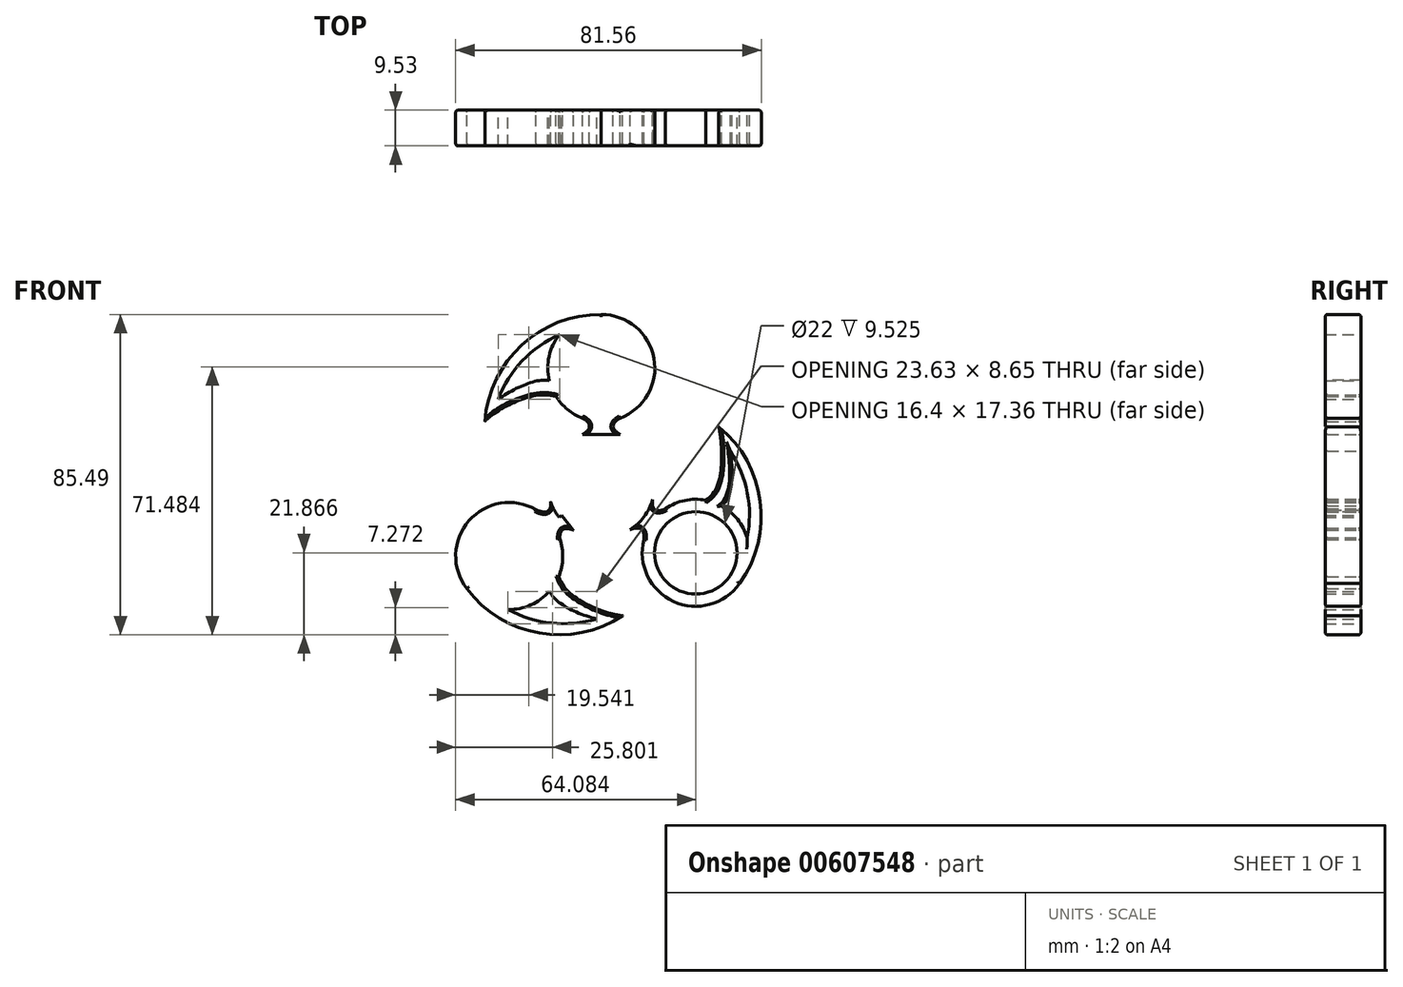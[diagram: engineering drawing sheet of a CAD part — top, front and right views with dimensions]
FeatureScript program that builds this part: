
annotation { "Feature Type Name" : "Feature", "Feature Type Description" : "" }
export const myFeature = defineFeature(function(context is Context, id is Id, definition is map)
    precondition{}
    {
        {
            var Q0;
            Q0=qCreatedBy(makeId("Front.planeOp"),FACE);
            var sketch = newSketch(context, id + "F0", { "sketchPlane" : qUnion([Q0])});
            skCircle(sketch, "E0", {"center": v(0, 0) * mm, "radius": 14.29 * mm});
            skLineSegment(sketch, "E1", {"start": v(0, 0) * mm, "end": v(0, 14.29) * mm});
            skLineSegment(sketch, "E2", {"start": v(0, 0) * mm, "end": v(-11.3, -8.76) * mm});
            skLineSegment(sketch, "E3", {"start": v(0, 0) * mm, "end": v(11.43, -8.57) * mm});
            skCircle(sketch, "E4", {"center": v(0, 31.12) * mm, "radius": 14.29 * mm});
            skLineSegment(sketch, "E5", {"start": v(0, 14.29) * mm, "end": v(0, 16.83) * mm});
            skArc(sketch, "E6", {"start": v(0, 45.4) * mm, "mid": v(-21.2, 37.27) * mm, "end": v(-31.1, 16.83) * mm});
            skFitSpline(sketch, "E7", {"points": [v(-31.1, 16.83) * mm, v(-17.35, 23.79) * mm, v(0, 16.83) * mm], "startDerivative": vector(18.3, 19.68) * mm, "endDerivative": vector(52.34, -33.11) * mm});
            skLineSegment(sketch, "E8", {"start": v(0, 15.56) * mm, "end": v(-3.18, 15.56) * mm});
            skPoint(sketch, "E8.endSnap0", {"position": v(0, 15.56) * mm});
            skLineSegment(sketch, "E9", {"start": v(0, 15.56) * mm, "end": v(3.18, 15.56) * mm});
            skLineSegment(sketch, "E10", {"start": v(0, 17.74) * mm, "end": v(5.03, 17.74) * mm});
            skLineSegment(sketch, "E11", {"start": v(0, 17.74) * mm, "end": v(-5.03, 17.74) * mm});
            skLineSegment(sketch, "E12", {"start": v(0, 14.29) * mm, "end": v(0, 13.37) * mm});
            skLineSegment(sketch, "E13", {"start": v(0, 13.37) * mm, "end": v(-5.03, 13.37) * mm});
            skLineSegment(sketch, "E14", {"start": v(0, 13.37) * mm, "end": v(5.03, 13.37) * mm});
            skFitSpline(sketch, "E15", {"points": [v(-5.03, 17.74) * mm, v(-3.18, 15.56) * mm, v(-5.03, 13.37) * mm], "startDerivative": vector(7.47, -4.37) * mm, "endDerivative": vector(-7.47, -4.37) * mm});
            skFitSpline(sketch, "E16", {"points": [v(5.03, 13.37) * mm, v(3.18, 15.56) * mm, v(5.03, 17.74) * mm], "startDerivative": vector(-7.47, 4.37) * mm, "endDerivative": vector(7.47, 4.37) * mm});
            skArc(sketch, "E17", {"start": v(4.36, 42.56) * mm, "mid": v(-16.61, 36.94) * mm, "end": v(-28.69, 18.9) * mm});
            skFitSpline(sketch, "E18", {"points": [v(-30.7, 19.98) * mm, v(-16.8, 27.72) * mm, v(0.44, 19.97) * mm], "startDerivative": vector(18.3, 19.68) * mm, "endDerivative": vector(52.34, -33.11) * mm});
            skLineSegment(sketch, "E19", {"start": v(-3.18, 15.56) * mm, "end": v(0, 14.29) * mm});
            skLineSegment(sketch, "E20", {"start": v(0, 14.29) * mm, "end": v(3.18, 15.56) * mm});
            skCircle(sketch, "E21", {"center": v(25.21, -18.22) * mm, "radius": 14.29 * mm});
            skLineSegment(sketch, "E22", {"start": v(11.43, -8.57) * mm, "end": v(13.51, -10.03) * mm});
            skArc(sketch, "E23", {"start": v(36.92, -26.42) * mm, "mid": v(42.42, -4.39) * mm, "end": v(31.34, 15.44) * mm});
            skFitSpline(sketch, "E24", {"points": [v(31.34, 15.44) * mm, v(30.71, -0.93) * mm, v(13.51, -10.03) * mm], "startDerivative": vector(5.62, -26.28) * mm, "endDerivative": vector(-57.15, -23.88) * mm});
            skLineSegment(sketch, "E25", {"start": v(12.47, -9.3) * mm, "end": v(14.3, -6.7) * mm});
            skPoint(sketch, "E25.endSnap0", {"position": v(12.47, -9.3) * mm});
            skLineSegment(sketch, "E26", {"start": v(12.47, -9.3) * mm, "end": v(10.65, -11.9) * mm});
            skLineSegment(sketch, "E27", {"start": v(14.26, -10.55) * mm, "end": v(11.38, -14.67) * mm});
            skLineSegment(sketch, "E28", {"start": v(14.26, -10.55) * mm, "end": v(17.14, -6.43) * mm});
            skArc(sketch, "E29", {"start": v(32.04, -28.23) * mm, "mid": v(39.54, -7.93) * mm, "end": v(31.84, 12.3) * mm});
            skFitSpline(sketch, "E30", {"points": [v(33.7, 13.3) * mm, v(33.83, -3.4) * mm, v(15.84, -12.2) * mm], "startDerivative": vector(5.62, -26.28) * mm, "endDerivative": vector(-57.15, -23.88) * mm});
            skLineSegment(sketch, "E31", {"start": v(14.3, -6.7) * mm, "end": v(11.8, -8.05) * mm});
            skLineSegment(sketch, "E32", {"start": v(11.43, -8.57) * mm, "end": v(10.65, -11.9) * mm});
            skLineSegment(sketch, "E33.0", {"start": v(14.3, -6.7) * mm, "end": v(12.47, -9.3) * mm, "construction": true});
            skCircle(sketch, "E34", {"center": v(-24.58, -19.07) * mm, "radius": 14.29 * mm});
            skLineSegment(sketch, "E35", {"start": v(-11.3, -8.76) * mm, "end": v(-13.26, -10.36) * mm});
            skArc(sketch, "E36", {"start": v(-35.91, -27.78) * mm, "mid": v(-16.54, -39.63) * mm, "end": v(5.7, -35.02) * mm});
            skFitSpline(sketch, "E37", {"points": [v(5.7, -35.02) * mm, v(-8.63, -28.76) * mm, v(-13.26, -10.36) * mm], "startDerivative": vector(-26.76, 2.52) * mm, "endDerivative": vector(-5.64, 61.68) * mm});
            skLineSegment(sketch, "E38", {"start": v(-12.27, -9.56) * mm, "end": v(-10.26, -12.02) * mm});
            skPoint(sketch, "E38.endSnap0", {"position": v(-12.27, -9.56) * mm});
            skLineSegment(sketch, "E39", {"start": v(-12.27, -9.56) * mm, "end": v(-14.28, -7.1) * mm});
            skLineSegment(sketch, "E40", {"start": v(-13.97, -10.94) * mm, "end": v(-17.43, -6.7) * mm});
            skLineSegment(sketch, "E41", {"start": v(-13.97, -10.94) * mm, "end": v(-11.04, -14.51) * mm});
            skArc(sketch, "E42", {"start": v(-36.27, -22.58) * mm, "mid": v(-19.07, -35.8) * mm, "end": v(2.57, -34.43) * mm});
            skFitSpline(sketch, "E43", {"points": [v(2.95, -36.62) * mm, v(-12.05, -30.77) * mm, v(-16.16, -11.65) * mm], "startDerivative": vector(-26.76, 2.52) * mm, "endDerivative": vector(-5.64, 61.68) * mm});
            skLineSegment(sketch, "E44", {"start": v(-10.26, -12.02) * mm, "end": v(-10.8, -9.23) * mm});
            skLineSegment(sketch, "E45", {"start": v(-11.3, -8.76) * mm, "end": v(-14.28, -7.1) * mm});
            skLineSegment(sketch, "E46.0", {"start": v(-10.26, -12.02) * mm, "end": v(-12.27, -9.56) * mm, "construction": true});
            skLineSegment(sketch, "E47", {"start": v(-11.3, -8.76) * mm, "end": v(-10.57, -8.2) * mm});
            skLineSegment(sketch, "E48", {"start": v(11.43, -8.57) * mm, "end": v(10.7, -8.02) * mm});
            skLineSegment(sketch, "E49", {"start": v(10.7, -8.02) * mm, "end": v(13.72, -4) * mm});
            skLineSegment(sketch, "E50", {"start": v(10.7, -8.02) * mm, "end": v(7.68, -12.05) * mm});
            skLineSegment(sketch, "E51", {"start": v(-10.57, -8.2) * mm, "end": v(-13.54, -4.56) * mm});
            skLineSegment(sketch, "E52", {"start": v(-10.57, -8.2) * mm, "end": v(-7.49, -12.17) * mm});
            skFitSpline(sketch, "E53", {"points": [v(-13.54, -4.56) * mm, v(-14.28, -7.1) * mm, v(-17.43, -6.7) * mm], "startDerivative": vector(0.73, -8.28) * mm, "endDerivative": vector(-8.38, 3.81) * mm});
            skFitSpline(sketch, "E54", {"points": [v(-11.04, -14.51) * mm, v(-10.26, -12.02) * mm, v(-7.49, -12.17) * mm], "startDerivative": vector(-0.57, 7.9) * mm, "endDerivative": vector(7.64, -3.14) * mm});
            skFitSpline(sketch, "E55", {"points": [v(7.68, -12.05) * mm, v(10.65, -11.9) * mm, v(11.38, -14.67) * mm], "startDerivative": vector(8.1, 3.32) * mm, "endDerivative": vector(-0.74, -8.6) * mm});
            skFitSpline(sketch, "E56", {"points": [v(13.72, -4) * mm, v(14.3, -6.7) * mm, v(17.14, -6.43) * mm], "startDerivative": vector(-1.06, -8.48) * mm, "endDerivative": vector(7.9, 3.59) * mm});
            skSolve(sketch);
        }
        {
            var Q0;
            {var subQ0=sQuery(id+"F0.wireOp",EDGE,"E6");var subQ1=sQuery(id+"F0.wireOp",EDGE,"E4");var subQ2=makeQuery(id+"F0.imprint","INTERSECT",VERTEX,{"derivedFrom":[subQ1,subQ0]});Q0=makeQuery(id+"F0.imprint","IMPRINT",FACE,{"disambiguationData":[TD([[makeQuery(id+"F0.imprint","IMPRINT",EDGE,{"disambiguationData":[TD([[subQ2,-1.0]])],"derivedFrom":subQ1}),-1.0]])]});}
            var Q1;
            {var subQ0=sQuery(id+"F0.wireOp",EDGE,"E18");var subQ1=sQuery(id+"F0.wireOp",EDGE,"E4");var subQ2=makeQuery(id+"F0.imprint","INTERSECT",VERTEX,{"derivedFrom":[subQ1,subQ0]});Q1=makeQuery(id+"F0.imprint","IMPRINT",FACE,{"disambiguationData":[TD([[makeQuery(id+"F0.imprint","IMPRINT",EDGE,{"disambiguationData":[TD([[subQ2,-1.0]])],"derivedFrom":subQ1}),-1.0]])]});}
            var Q2;
            {var subQ0=sQuery(id+"F0.wireOp",EDGE,"E7");var subQ1=sQuery(id+"F0.wireOp",EDGE,"E6");var subQ2=makeQuery(id+"F0.imprint","INTERSECT",VERTEX,{"derivedFrom":[subQ1,subQ0]});Q2=makeQuery(id+"F0.imprint","IMPRINT",FACE,{"disambiguationData":[TD([[makeQuery(id+"F0.imprint","IMPRINT",EDGE,{"disambiguationData":[TD([[subQ2,1.0]])],"derivedFrom":subQ1}),1.0]])]});}
            var Q3;
            {var subQ7=sQuery(id+"F0.wireOp",EDGE,"E10");Q3=makeQuery(id+"F0.imprint","IMPRINT",FACE,{"disambiguationData":[TD([[makeQuery(id+"F0.imprint","IMPRINT",EDGE,{"derivedFrom":subQ7}),1.0]])]});}
            var Q4;
            Q4=makeQuery(id+"F0.imprint","IMPRINT",FACE,{"disambiguationData":[TD([[makeQuery(id+"F0.imprint","IMPRINT",EDGE,{"derivedFrom":sQuery(id+"F0.wireOp",EDGE,"E1")}),1.0]])]});
            var Q5;
            Q5=makeQuery(id+"F0.imprint","IMPRINT",FACE,{"disambiguationData":[TD([[makeQuery(id+"F0.imprint","IMPRINT",EDGE,{"derivedFrom":sQuery(id+"F0.wireOp",EDGE,"E2")}),1.0]])]});
            var Q6;
            Q6=makeQuery(id+"F0.imprint","IMPRINT",FACE,{"disambiguationData":[TD([[makeQuery(id+"F0.imprint","IMPRINT",EDGE,{"derivedFrom":sQuery(id+"F0.wireOp",EDGE,"E1")}),-1.0]])]});
            var Q7;
            {var subQ7=sQuery(id+"F0.wireOp",EDGE,"E40");Q7=makeQuery(id+"F0.imprint","IMPRINT",FACE,{"disambiguationData":[TD([[makeQuery(id+"F0.imprint","IMPRINT",EDGE,{"derivedFrom":subQ7}),1.0]])]});}
            var Q8;
            {var subQ0=sQuery(id+"F0.wireOp",EDGE,"E36");var subQ1=sQuery(id+"F0.wireOp",EDGE,"E34");var subQ2=makeQuery(id+"F0.imprint","INTERSECT",VERTEX,{"derivedFrom":[subQ1,subQ0]});Q8=makeQuery(id+"F0.imprint","IMPRINT",FACE,{"disambiguationData":[TD([[makeQuery(id+"F0.imprint","IMPRINT",EDGE,{"disambiguationData":[TD([[subQ2,-1.0]])],"derivedFrom":subQ1}),-1.0]])]});}
            var Q9;
            {var subQ0=sQuery(id+"F0.wireOp",EDGE,"E43");var subQ1=sQuery(id+"F0.wireOp",EDGE,"E34");var subQ2=makeQuery(id+"F0.imprint","INTERSECT",VERTEX,{"derivedFrom":[subQ1,subQ0]});Q9=makeQuery(id+"F0.imprint","IMPRINT",FACE,{"disambiguationData":[TD([[makeQuery(id+"F0.imprint","IMPRINT",EDGE,{"disambiguationData":[TD([[subQ2,-1.0]])],"derivedFrom":subQ1}),-1.0]])]});}
            var Q10;
            {var subQ0=sQuery(id+"F0.wireOp",EDGE,"E37");var subQ1=sQuery(id+"F0.wireOp",EDGE,"E36");var subQ2=makeQuery(id+"F0.imprint","INTERSECT",VERTEX,{"derivedFrom":[subQ1,subQ0]});Q10=makeQuery(id+"F0.imprint","IMPRINT",FACE,{"disambiguationData":[TD([[makeQuery(id+"F0.imprint","IMPRINT",EDGE,{"disambiguationData":[TD([[subQ2,1.0]])],"derivedFrom":subQ1}),1.0]])]});}
            var Q11;
            {var subQ1=sQuery(id+"F0.wireOp",EDGE,"E34");var subQ3=sQuery(id+"F0.wireOp",EDGE,"E37");var subQ4=makeQuery(id+"F0.imprint","INTERSECT",VERTEX,{"derivedFrom":[subQ1,subQ3]});Q11=makeQuery(id+"F0.imprint","IMPRINT",FACE,{"disambiguationData":[TD([[makeQuery(id+"F0.imprint","IMPRINT",EDGE,{"disambiguationData":[TD([[subQ4,-1.0]])],"derivedFrom":subQ3}),-1.0]])]});}
            var Q12;
            {var subQ5=sQuery(id+"F0.wireOp",EDGE,"E27");Q12=makeQuery(id+"F0.imprint","IMPRINT",FACE,{"disambiguationData":[TD([[makeQuery(id+"F0.imprint","IMPRINT",EDGE,{"derivedFrom":subQ5}),1.0]])]});}
            var Q13;
            {var subQ0=sQuery(id+"F0.wireOp",EDGE,"E23");var subQ1=sQuery(id+"F0.wireOp",EDGE,"E21");var subQ2=makeQuery(id+"F0.imprint","INTERSECT",VERTEX,{"derivedFrom":[subQ1,subQ0]});Q13=makeQuery(id+"F0.imprint","IMPRINT",FACE,{"disambiguationData":[TD([[makeQuery(id+"F0.imprint","IMPRINT",EDGE,{"disambiguationData":[TD([[subQ2,-1.0]])],"derivedFrom":subQ1}),-1.0]])]});}
            var Q14;
            {var subQ0=sQuery(id+"F0.wireOp",EDGE,"E30");var subQ1=sQuery(id+"F0.wireOp",EDGE,"E21");var subQ2=makeQuery(id+"F0.imprint","INTERSECT",VERTEX,{"derivedFrom":[subQ1,subQ0]});Q14=makeQuery(id+"F0.imprint","IMPRINT",FACE,{"disambiguationData":[TD([[makeQuery(id+"F0.imprint","IMPRINT",EDGE,{"disambiguationData":[TD([[subQ2,-1.0]])],"derivedFrom":subQ1}),-1.0]])]});}
            var Q15;
            {var subQ0=sQuery(id+"F0.wireOp",EDGE,"E24");var subQ1=sQuery(id+"F0.wireOp",EDGE,"E23");var subQ2=makeQuery(id+"F0.imprint","INTERSECT",VERTEX,{"derivedFrom":[subQ1,subQ0]});Q15=makeQuery(id+"F0.imprint","IMPRINT",FACE,{"disambiguationData":[TD([[makeQuery(id+"F0.imprint","IMPRINT",EDGE,{"disambiguationData":[TD([[subQ2,1.0]])],"derivedFrom":subQ1}),1.0]])]});}
            var Q16;
            {var subQ0=sQuery(id+"F0.wireOp",EDGE,"E28");var subQ1=sQuery(id+"F0.wireOp",EDGE,"E21");var subQ2=makeQuery(id+"F0.imprint","INTERSECT",VERTEX,{"derivedFrom":[subQ1,subQ0]});Q16=makeQuery(id+"F0.imprint","IMPRINT",FACE,{"disambiguationData":[TD([[makeQuery(id+"F0.imprint","IMPRINT",EDGE,{"disambiguationData":[TD([[subQ2,1.0]])],"derivedFrom":subQ1}),1.0]])]});}
            var Q17;
            {var subQ3=sQuery(id+"F0.wireOp",EDGE,"E40");Q17=makeQuery(id+"F0.imprint","IMPRINT",FACE,{"disambiguationData":[TD([[makeQuery(id+"F0.imprint","IMPRINT",EDGE,{"derivedFrom":subQ3}),-1.0]])]});}
            var Q18;
            {var subQ0=sQuery(id+"F0.wireOp",EDGE,"E37");var subQ3=sQuery(id+"F0.wireOp",EDGE,"E41");var subQ5=makeQuery(id+"F0.imprint","INTERSECT",VERTEX,{"derivedFrom":[subQ0,subQ3]});Q18=makeQuery(id+"F0.imprint","IMPRINT",FACE,{"disambiguationData":[TD([[makeQuery(id+"F0.imprint","IMPRINT",EDGE,{"disambiguationData":[TD([[subQ5,-1.0]])],"derivedFrom":subQ0}),-1.0]])]});}
            var Q19;
            {var subQ0=sQuery(id+"F0.wireOp",EDGE,"E47");Q19=makeQuery(id+"F0.imprint","IMPRINT",FACE,{"disambiguationData":[TD([[makeQuery(id+"F0.imprint","IMPRINT",EDGE,{"derivedFrom":subQ0}),-1.0]])]});}
            var Q20;
            {var subQ0=sQuery(id+"F0.wireOp",EDGE,"E47");Q20=makeQuery(id+"F0.imprint","IMPRINT",FACE,{"disambiguationData":[TD([[makeQuery(id+"F0.imprint","IMPRINT",EDGE,{"derivedFrom":subQ0}),1.0]])]});}
            var Q21;
            {var subQ0=sQuery(id+"F0.wireOp",EDGE,"E45");Q21=makeQuery(id+"F0.imprint","IMPRINT",FACE,{"disambiguationData":[TD([[makeQuery(id+"F0.imprint","IMPRINT",EDGE,{"derivedFrom":subQ0}),-1.0]])]});}
            var Q22;
            {var subQ1=sQuery(id+"F0.wireOp",EDGE,"E0");var subQ3=sQuery(id+"F0.wireOp",EDGE,"E44");var subQ4=makeQuery(id+"F0.imprint","INTERSECT",VERTEX,{"derivedFrom":[subQ1,subQ3]});Q22=makeQuery(id+"F0.imprint","IMPRINT",FACE,{"disambiguationData":[TD([[makeQuery(id+"F0.imprint","IMPRINT",EDGE,{"disambiguationData":[TD([[subQ4,-1.0]])],"derivedFrom":subQ1}),-1.0]])]});}
            var Q23;
            {var subQ5=sQuery(id+"F0.wireOp",EDGE,"E38");Q23=makeQuery(id+"F0.imprint","IMPRINT",FACE,{"disambiguationData":[TD([[makeQuery(id+"F0.imprint","IMPRINT",EDGE,{"derivedFrom":subQ5}),-1.0]])]});}
            var Q24;
            {var subQ5=sQuery(id+"F0.wireOp",EDGE,"E39");Q24=makeQuery(id+"F0.imprint","IMPRINT",FACE,{"disambiguationData":[TD([[makeQuery(id+"F0.imprint","IMPRINT",EDGE,{"derivedFrom":subQ5}),1.0]])]});}
            var Q25;
            {var subQ2=sQuery(id+"F0.wireOp",EDGE,"E39");Q25=makeQuery(id+"F0.imprint","IMPRINT",FACE,{"disambiguationData":[TD([[makeQuery(id+"F0.imprint","IMPRINT",EDGE,{"derivedFrom":subQ2}),-1.0]])]});}
            var Q26;
            {var subQ5=sQuery(id+"F0.wireOp",EDGE,"E38");Q26=makeQuery(id+"F0.imprint","IMPRINT",FACE,{"disambiguationData":[TD([[makeQuery(id+"F0.imprint","IMPRINT",EDGE,{"derivedFrom":subQ5}),1.0]])]});}
            var Q27;
            {var subQ3=sQuery(id+"F0.wireOp",EDGE,"E27");Q27=makeQuery(id+"F0.imprint","IMPRINT",FACE,{"disambiguationData":[TD([[makeQuery(id+"F0.imprint","IMPRINT",EDGE,{"derivedFrom":subQ3}),-1.0]])]});}
            var Q28;
            {var subQ0=sQuery(id+"F0.wireOp",EDGE,"E24");var subQ3=sQuery(id+"F0.wireOp",EDGE,"E28");var subQ5=makeQuery(id+"F0.imprint","INTERSECT",VERTEX,{"derivedFrom":[subQ0,subQ3]});Q28=makeQuery(id+"F0.imprint","IMPRINT",FACE,{"disambiguationData":[TD([[makeQuery(id+"F0.imprint","IMPRINT",EDGE,{"disambiguationData":[TD([[subQ5,-1.0]])],"derivedFrom":subQ0}),-1.0]])]});}
            var Q29;
            {var subQ5=sQuery(id+"F0.wireOp",EDGE,"E25");Q29=makeQuery(id+"F0.imprint","IMPRINT",FACE,{"disambiguationData":[TD([[makeQuery(id+"F0.imprint","IMPRINT",EDGE,{"derivedFrom":subQ5}),-1.0]])]});}
            var Q30;
            {var subQ2=sQuery(id+"F0.wireOp",EDGE,"E25");Q30=makeQuery(id+"F0.imprint","IMPRINT",FACE,{"disambiguationData":[TD([[makeQuery(id+"F0.imprint","IMPRINT",EDGE,{"derivedFrom":subQ2}),1.0]])]});}
            var Q31;
            {var subQ0=sQuery(id+"F0.wireOp",EDGE,"E31");Q31=makeQuery(id+"F0.imprint","IMPRINT",FACE,{"disambiguationData":[TD([[makeQuery(id+"F0.imprint","IMPRINT",EDGE,{"derivedFrom":subQ0}),-1.0]])]});}
            var Q32;
            {var subQ0=sQuery(id+"F0.wireOp",EDGE,"E48");Q32=makeQuery(id+"F0.imprint","IMPRINT",FACE,{"disambiguationData":[TD([[makeQuery(id+"F0.imprint","IMPRINT",EDGE,{"derivedFrom":subQ0}),-1.0]])]});}
            var Q33;
            {var subQ0=sQuery(id+"F0.wireOp",EDGE,"E48");Q33=makeQuery(id+"F0.imprint","IMPRINT",FACE,{"disambiguationData":[TD([[makeQuery(id+"F0.imprint","IMPRINT",EDGE,{"derivedFrom":subQ0}),1.0]])]});}
            var Q34;
            {var subQ0=sQuery(id+"F0.wireOp",EDGE,"E32");Q34=makeQuery(id+"F0.imprint","IMPRINT",FACE,{"disambiguationData":[TD([[makeQuery(id+"F0.imprint","IMPRINT",EDGE,{"derivedFrom":subQ0}),-1.0]])]});}
            var Q35;
            {var subQ2=sQuery(id+"F0.wireOp",EDGE,"E26");Q35=makeQuery(id+"F0.imprint","IMPRINT",FACE,{"disambiguationData":[TD([[makeQuery(id+"F0.imprint","IMPRINT",EDGE,{"derivedFrom":subQ2}),-1.0]])]});}
            var Q36;
            {var subQ5=sQuery(id+"F0.wireOp",EDGE,"E26");Q36=makeQuery(id+"F0.imprint","IMPRINT",FACE,{"disambiguationData":[TD([[makeQuery(id+"F0.imprint","IMPRINT",EDGE,{"derivedFrom":subQ5}),1.0]])]});}
            var Q37;
            {var subQ1=sQuery(id+"F0.wireOp",EDGE,"E4");var subQ3=sQuery(id+"F0.wireOp",EDGE,"E7");var subQ4=makeQuery(id+"F0.imprint","INTERSECT",VERTEX,{"derivedFrom":[subQ1,subQ3]});Q37=makeQuery(id+"F0.imprint","IMPRINT",FACE,{"disambiguationData":[TD([[makeQuery(id+"F0.imprint","IMPRINT",EDGE,{"disambiguationData":[TD([[subQ4,-1.0]])],"derivedFrom":subQ3}),-1.0]])]});}
            var Q38;
            {var subQ0=sQuery(id+"F0.wireOp",EDGE,"E7");var subQ3=sQuery(id+"F0.wireOp",EDGE,"E11");var subQ5=makeQuery(id+"F0.imprint","INTERSECT",VERTEX,{"derivedFrom":[subQ0,subQ3]});Q38=makeQuery(id+"F0.imprint","IMPRINT",FACE,{"disambiguationData":[TD([[makeQuery(id+"F0.imprint","IMPRINT",EDGE,{"disambiguationData":[TD([[subQ5,-1.0]])],"derivedFrom":subQ0}),-1.0]])]});}
            var Q39;
            {var subQ5=sQuery(id+"F0.wireOp",EDGE,"E8");Q39=makeQuery(id+"F0.imprint","IMPRINT",FACE,{"disambiguationData":[TD([[makeQuery(id+"F0.imprint","IMPRINT",EDGE,{"derivedFrom":subQ5}),-1.0]])]});}
            var Q40;
            {var subQ0=sQuery(id+"F0.wireOp",EDGE,"E20");Q40=makeQuery(id+"F0.imprint","IMPRINT",FACE,{"disambiguationData":[TD([[makeQuery(id+"F0.imprint","IMPRINT",EDGE,{"derivedFrom":subQ0}),-1.0]])]});}
            var Q41;
            {var subQ0=sQuery(id+"F0.wireOp",EDGE,"E12");Q41=makeQuery(id+"F0.imprint","IMPRINT",FACE,{"disambiguationData":[TD([[makeQuery(id+"F0.imprint","IMPRINT",EDGE,{"derivedFrom":subQ0}),1.0]])]});}
            var Q42;
            {var subQ0=sQuery(id+"F0.wireOp",EDGE,"E12");Q42=makeQuery(id+"F0.imprint","IMPRINT",FACE,{"disambiguationData":[TD([[makeQuery(id+"F0.imprint","IMPRINT",EDGE,{"derivedFrom":subQ0}),-1.0]])]});}
            var Q43;
            {var subQ0=sQuery(id+"F0.wireOp",EDGE,"E19");Q43=makeQuery(id+"F0.imprint","IMPRINT",FACE,{"disambiguationData":[TD([[makeQuery(id+"F0.imprint","IMPRINT",EDGE,{"derivedFrom":subQ0}),-1.0]])]});}
            var Q44;
            {var subQ2=sQuery(id+"F0.wireOp",EDGE,"E8");Q44=makeQuery(id+"F0.imprint","IMPRINT",FACE,{"disambiguationData":[TD([[makeQuery(id+"F0.imprint","IMPRINT",EDGE,{"derivedFrom":subQ2}),1.0]])]});}
            var Q45;
            {var subQ2=sQuery(id+"F0.wireOp",EDGE,"E9");Q45=makeQuery(id+"F0.imprint","IMPRINT",FACE,{"disambiguationData":[TD([[makeQuery(id+"F0.imprint","IMPRINT",EDGE,{"derivedFrom":subQ2}),-1.0]])]});}
            var Q46;
            {var subQ5=sQuery(id+"F0.wireOp",EDGE,"E9");Q46=makeQuery(id+"F0.imprint","IMPRINT",FACE,{"disambiguationData":[TD([[makeQuery(id+"F0.imprint","IMPRINT",EDGE,{"derivedFrom":subQ5}),1.0]])]});}
            var Q47;
            {var subQ3=sQuery(id+"F0.wireOp",EDGE,"E10");Q47=makeQuery(id+"F0.imprint","IMPRINT",FACE,{"disambiguationData":[TD([[makeQuery(id+"F0.imprint","IMPRINT",EDGE,{"derivedFrom":subQ3}),-1.0]])]});}
            extrude(context, id + "F1", {"entities" : qUnion([Q0, Q1, Q2, Q3, Q4, Q5, Q6, Q7, Q8, Q9, Q10, Q11, Q12, Q13, Q14, Q15, Q16, Q17, Q18, Q19, Q20, Q21, Q22, Q23, Q24, Q25, Q26, Q27, Q28, Q29, Q30, Q31, Q32, Q33, Q34, Q35, Q36, Q37, Q38, Q39, Q40, Q41, Q42, Q43, Q44, Q45, Q46, Q47]), "depth" : 9.52 * mm});
        }
        {
            var Q0;
            {var subQ0=sQuery(id+"F0.wireOp",EDGE,"E4");Q0=makeQuery(id+"F1.opExtrude","CAP_EDGE",EDGE,{"disambiguationData":[OSD([subQ0]),TDD([makeQuery(id+"F0.imprint","IMPRINT",EDGE,{"disambiguationData":[TD([[makeQuery(id+"F0.imprint","INTERSECT",VERTEX,{"derivedFrom":[subQ0,sQuery(id+"F0.wireOp",EDGE,"E7")]}),-1.0]])],"derivedFrom":subQ0})])],"isStart":false});}
            var Q1;
            Q1=makeQuery(id+"F1.opExtrude","CAP_EDGE",EDGE,{"disambiguationData":[OSD([sQuery(id+"F0.wireOp",EDGE,"E15")])],"isStart":false});
            var Q2;
            {var subQ0=sQuery(id+"F0.wireOp",EDGE,"E0");Q2=makeQuery(id+"F1.opExtrude","CAP_EDGE",EDGE,{"disambiguationData":[OSD([subQ0]),TDD([makeQuery(id+"F0.imprint","IMPRINT",EDGE,{"disambiguationData":[TD([[makeQuery(id+"F0.imprint","INTERSECT",VERTEX,{"derivedFrom":[subQ0,sQuery(id+"F0.wireOp",EDGE,"E13"),sQuery(id+"F0.wireOp",EDGE,"E15")]}),-1.0]])],"derivedFrom":subQ0})])],"isStart":false});}
            var Q3;
            Q3=makeQuery(id+"F1.opExtrude","CAP_EDGE",EDGE,{"disambiguationData":[OSD([sQuery(id+"F0.wireOp",EDGE,"E53")])],"isStart":false});
            var Q4;
            {var subQ0=sQuery(id+"F0.wireOp",EDGE,"E34");Q4=makeQuery(id+"F1.opExtrude","CAP_EDGE",EDGE,{"disambiguationData":[OSD([subQ0]),TDD([makeQuery(id+"F0.imprint","IMPRINT",EDGE,{"disambiguationData":[TD([[makeQuery(id+"F0.imprint","INTERSECT",VERTEX,{"derivedFrom":[subQ0,sQuery(id+"F0.wireOp",EDGE,"E36")]}),1.0]])],"derivedFrom":subQ0})])],"isStart":false});}
            var Q5;
            Q5=makeQuery(id+"F1.opExtrude","CAP_EDGE",EDGE,{"disambiguationData":[OSD([sQuery(id+"F0.wireOp",EDGE,"E36")])],"isStart":false});
            var Q6;
            Q6=makeQuery(id+"F1.opExtrude","CAP_EDGE",EDGE,{"disambiguationData":[OSD([sQuery(id+"F0.wireOp",EDGE,"E37")])],"isStart":false});
            var Q7;
            Q7=makeQuery(id+"F1.opExtrude","CAP_FACE",FACE,{"disambiguationData":[OSD([sQuery(id+"F0.wireOp",EDGE,"E0"),sQuery(id+"F0.wireOp",EDGE,"E4"),sQuery(id+"F0.wireOp",EDGE,"E6"),sQuery(id+"F0.wireOp",EDGE,"E7"),sQuery(id+"F0.wireOp",EDGE,"E15"),sQuery(id+"F0.wireOp",EDGE,"E16"),sQuery(id+"F0.wireOp",EDGE,"E17"),sQuery(id+"F0.wireOp",EDGE,"E18"),sQuery(id+"F0.wireOp",EDGE,"E21"),sQuery(id+"F0.wireOp",EDGE,"E23"),sQuery(id+"F0.wireOp",EDGE,"E24"),sQuery(id+"F0.wireOp",EDGE,"E29"),sQuery(id+"F0.wireOp",EDGE,"E30"),sQuery(id+"F0.wireOp",EDGE,"E34"),sQuery(id+"F0.wireOp",EDGE,"E36"),sQuery(id+"F0.wireOp",EDGE,"E37"),sQuery(id+"F0.wireOp",EDGE,"E42"),sQuery(id+"F0.wireOp",EDGE,"E43"),sQuery(id+"F0.wireOp",EDGE,"E53"),sQuery(id+"F0.wireOp",EDGE,"E54"),sQuery(id+"F0.wireOp",EDGE,"E55"),sQuery(id+"F0.wireOp",EDGE,"E56")])],"isStart":false});
            var Q8;
            Q8=makeQuery(id+"F1.opExtrude","CAP_EDGE",EDGE,{"disambiguationData":[OSD([sQuery(id+"F0.wireOp",EDGE,"E7")])],"isStart":false});
            var Q9;
            Q9=makeQuery(id+"F1.opExtrude","CAP_EDGE",EDGE,{"disambiguationData":[OSD([sQuery(id+"F0.wireOp",EDGE,"E54")])],"isStart":false});
            var Q10;
            {var subQ0=sQuery(id+"F0.wireOp",EDGE,"E34");Q10=makeQuery(id+"F1.opExtrude","CAP_EDGE",EDGE,{"disambiguationData":[OSD([subQ0]),TDD([makeQuery(id+"F0.imprint","IMPRINT",EDGE,{"disambiguationData":[TD([[makeQuery(id+"F0.imprint","INTERSECT",VERTEX,{"derivedFrom":[subQ0,sQuery(id+"F0.wireOp",EDGE,"E37")]}),-1.0]])],"derivedFrom":subQ0})])],"isStart":false});}
            var Q11;
            {var subQ0=sQuery(id+"F0.wireOp",EDGE,"E0");Q11=makeQuery(id+"F1.opExtrude","CAP_EDGE",EDGE,{"disambiguationData":[OSD([subQ0]),TDD([makeQuery(id+"F0.imprint","IMPRINT",EDGE,{"disambiguationData":[TD([[makeQuery(id+"F0.imprint","INTERSECT",VERTEX,{"derivedFrom":[subQ0,sQuery(id+"F0.wireOp",EDGE,"E50"),sQuery(id+"F0.wireOp",EDGE,"E55")]}),1.0]])],"derivedFrom":subQ0})])],"isStart":false});}
            var Q12;
            Q12=makeQuery(id+"F1.opExtrude","CAP_EDGE",EDGE,{"disambiguationData":[OSD([sQuery(id+"F0.wireOp",EDGE,"E55")])],"isStart":false});
            var Q13;
            {var subQ0=sQuery(id+"F0.wireOp",EDGE,"E21");Q13=makeQuery(id+"F1.opExtrude","CAP_EDGE",EDGE,{"disambiguationData":[OSD([subQ0]),TDD([makeQuery(id+"F0.imprint","IMPRINT",EDGE,{"disambiguationData":[TD([[makeQuery(id+"F0.imprint","INTERSECT",VERTEX,{"derivedFrom":[subQ0,sQuery(id+"F0.wireOp",EDGE,"E23")]}),1.0]])],"derivedFrom":subQ0})])],"isStart":false});}
            var Q14;
            Q14=makeQuery(id+"F1.opExtrude","CAP_EDGE",EDGE,{"disambiguationData":[OSD([sQuery(id+"F0.wireOp",EDGE,"E23")])],"isStart":false});
            var Q15;
            Q15=makeQuery(id+"F1.opExtrude","CAP_EDGE",EDGE,{"disambiguationData":[OSD([sQuery(id+"F0.wireOp",EDGE,"E24")])],"isStart":false});
            var Q16;
            {var subQ0=sQuery(id+"F0.wireOp",EDGE,"E21");Q16=makeQuery(id+"F1.opExtrude","CAP_EDGE",EDGE,{"disambiguationData":[OSD([subQ0]),TDD([makeQuery(id+"F0.imprint","IMPRINT",EDGE,{"disambiguationData":[TD([[makeQuery(id+"F0.imprint","INTERSECT",VERTEX,{"derivedFrom":[subQ0,sQuery(id+"F0.wireOp",EDGE,"E24")]}),-1.0]])],"derivedFrom":subQ0})])],"isStart":false});}
            var Q17;
            Q17=makeQuery(id+"F1.opExtrude","CAP_EDGE",EDGE,{"disambiguationData":[OSD([sQuery(id+"F0.wireOp",EDGE,"E56")])],"isStart":false});
            var Q18;
            {var subQ0=sQuery(id+"F0.wireOp",EDGE,"E0");Q18=makeQuery(id+"F1.opExtrude","CAP_EDGE",EDGE,{"disambiguationData":[OSD([subQ0]),TDD([makeQuery(id+"F0.imprint","IMPRINT",EDGE,{"disambiguationData":[TD([[makeQuery(id+"F0.imprint","INTERSECT",VERTEX,{"derivedFrom":[subQ0,sQuery(id+"F0.wireOp",EDGE,"E14"),sQuery(id+"F0.wireOp",EDGE,"E16")]}),1.0]])],"derivedFrom":subQ0})])],"isStart":false});}
            var Q19;
            Q19=makeQuery(id+"F1.opExtrude","CAP_EDGE",EDGE,{"disambiguationData":[OSD([sQuery(id+"F0.wireOp",EDGE,"E16")])],"isStart":false});
            var Q20;
            {var subQ0=sQuery(id+"F0.wireOp",EDGE,"E4");Q20=makeQuery(id+"F1.opExtrude","CAP_EDGE",EDGE,{"disambiguationData":[OSD([subQ0]),TDD([makeQuery(id+"F0.imprint","IMPRINT",EDGE,{"disambiguationData":[TD([[makeQuery(id+"F0.imprint","INTERSECT",VERTEX,{"derivedFrom":[subQ0,sQuery(id+"F0.wireOp",EDGE,"E6")]}),1.0]])],"derivedFrom":subQ0})])],"isStart":false});}
            var Q21;
            Q21=makeQuery(id+"F1.opExtrude","CAP_EDGE",EDGE,{"disambiguationData":[OSD([sQuery(id+"F0.wireOp",EDGE,"E6")])],"isStart":false});
            var Q22;
            Q22=makeQuery(id+"F1.opExtrude","CAP_EDGE",EDGE,{"disambiguationData":[OSD([sQuery(id+"F0.wireOp",EDGE,"E16")])],"isStart":true});
            var Q23;
            {var subQ0=sQuery(id+"F0.wireOp",EDGE,"E4");Q23=makeQuery(id+"F1.opExtrude","CAP_EDGE",EDGE,{"disambiguationData":[OSD([subQ0]),TDD([makeQuery(id+"F0.imprint","IMPRINT",EDGE,{"disambiguationData":[TD([[makeQuery(id+"F0.imprint","INTERSECT",VERTEX,{"derivedFrom":[subQ0,sQuery(id+"F0.wireOp",EDGE,"E6")]}),1.0]])],"derivedFrom":subQ0})])],"isStart":true});}
            var Q24;
            {var subQ0=sQuery(id+"F0.wireOp",EDGE,"E0");Q24=makeQuery(id+"F1.opExtrude","CAP_EDGE",EDGE,{"disambiguationData":[OSD([subQ0]),TDD([makeQuery(id+"F0.imprint","IMPRINT",EDGE,{"disambiguationData":[TD([[makeQuery(id+"F0.imprint","INTERSECT",VERTEX,{"derivedFrom":[subQ0,sQuery(id+"F0.wireOp",EDGE,"E14"),sQuery(id+"F0.wireOp",EDGE,"E16")]}),1.0]])],"derivedFrom":subQ0})])],"isStart":true});}
            var Q25;
            Q25=makeQuery(id+"F1.opExtrude","CAP_EDGE",EDGE,{"disambiguationData":[OSD([sQuery(id+"F0.wireOp",EDGE,"E56")])],"isStart":true});
            var Q26;
            {var subQ0=sQuery(id+"F0.wireOp",EDGE,"E21");Q26=makeQuery(id+"F1.opExtrude","CAP_EDGE",EDGE,{"disambiguationData":[OSD([subQ0]),TDD([makeQuery(id+"F0.imprint","IMPRINT",EDGE,{"disambiguationData":[TD([[makeQuery(id+"F0.imprint","INTERSECT",VERTEX,{"derivedFrom":[subQ0,sQuery(id+"F0.wireOp",EDGE,"E24")]}),-1.0]])],"derivedFrom":subQ0})])],"isStart":true});}
            var Q27;
            Q27=makeQuery(id+"F1.opExtrude","CAP_EDGE",EDGE,{"disambiguationData":[OSD([sQuery(id+"F0.wireOp",EDGE,"E23")])],"isStart":true});
            var Q28;
            Q28=makeQuery(id+"F1.opExtrude","CAP_EDGE",EDGE,{"disambiguationData":[OSD([sQuery(id+"F0.wireOp",EDGE,"E55")])],"isStart":true});
            var Q29;
            {var subQ0=sQuery(id+"F0.wireOp",EDGE,"E0");Q29=makeQuery(id+"F1.opExtrude","CAP_EDGE",EDGE,{"disambiguationData":[OSD([subQ0]),TDD([makeQuery(id+"F0.imprint","IMPRINT",EDGE,{"disambiguationData":[TD([[makeQuery(id+"F0.imprint","INTERSECT",VERTEX,{"derivedFrom":[subQ0,sQuery(id+"F0.wireOp",EDGE,"E50"),sQuery(id+"F0.wireOp",EDGE,"E55")]}),1.0]])],"derivedFrom":subQ0})])],"isStart":true});}
            var Q30;
            Q30=makeQuery(id+"F1.opExtrude","CAP_EDGE",EDGE,{"disambiguationData":[OSD([sQuery(id+"F0.wireOp",EDGE,"E54")])],"isStart":true});
            var Q31;
            {var subQ0=sQuery(id+"F0.wireOp",EDGE,"E34");Q31=makeQuery(id+"F1.opExtrude","CAP_EDGE",EDGE,{"disambiguationData":[OSD([subQ0]),TDD([makeQuery(id+"F0.imprint","IMPRINT",EDGE,{"disambiguationData":[TD([[makeQuery(id+"F0.imprint","INTERSECT",VERTEX,{"derivedFrom":[subQ0,sQuery(id+"F0.wireOp",EDGE,"E37")]}),-1.0]])],"derivedFrom":subQ0})])],"isStart":true});}
            var Q32;
            Q32=makeQuery(id+"F1.opExtrude","CAP_EDGE",EDGE,{"disambiguationData":[OSD([sQuery(id+"F0.wireOp",EDGE,"E37")])],"isStart":true});
            var Q33;
            Q33=makeQuery(id+"F1.opExtrude","CAP_EDGE",EDGE,{"disambiguationData":[OSD([sQuery(id+"F0.wireOp",EDGE,"E36")])],"isStart":true});
            var Q34;
            Q34=makeQuery(id+"F1.opExtrude","CAP_EDGE",EDGE,{"disambiguationData":[OSD([sQuery(id+"F0.wireOp",EDGE,"E36")])],"isStart":true});
            var Q35;
            {var subQ0=sQuery(id+"F0.wireOp",EDGE,"E34");Q35=makeQuery(id+"F1.opExtrude","CAP_EDGE",EDGE,{"disambiguationData":[OSD([subQ0]),TDD([makeQuery(id+"F0.imprint","IMPRINT",EDGE,{"disambiguationData":[TD([[makeQuery(id+"F0.imprint","INTERSECT",VERTEX,{"derivedFrom":[subQ0,sQuery(id+"F0.wireOp",EDGE,"E36")]}),1.0]])],"derivedFrom":subQ0})])],"isStart":true});}
            var Q36;
            Q36=makeQuery(id+"F1.opExtrude","CAP_EDGE",EDGE,{"disambiguationData":[OSD([sQuery(id+"F0.wireOp",EDGE,"E53")])],"isStart":true});
            var Q37;
            {var subQ0=sQuery(id+"F0.wireOp",EDGE,"E0");Q37=makeQuery(id+"F1.opExtrude","CAP_EDGE",EDGE,{"disambiguationData":[OSD([subQ0]),TDD([makeQuery(id+"F0.imprint","IMPRINT",EDGE,{"disambiguationData":[TD([[makeQuery(id+"F0.imprint","INTERSECT",VERTEX,{"derivedFrom":[subQ0,sQuery(id+"F0.wireOp",EDGE,"E13"),sQuery(id+"F0.wireOp",EDGE,"E15")]}),-1.0]])],"derivedFrom":subQ0})])],"isStart":true});}
            var Q38;
            Q38=makeQuery(id+"F1.opExtrude","CAP_EDGE",EDGE,{"disambiguationData":[OSD([sQuery(id+"F0.wireOp",EDGE,"E15")])],"isStart":true});
            var Q39;
            {var subQ0=sQuery(id+"F0.wireOp",EDGE,"E4");Q39=makeQuery(id+"F1.opExtrude","CAP_EDGE",EDGE,{"disambiguationData":[OSD([subQ0]),TDD([makeQuery(id+"F0.imprint","IMPRINT",EDGE,{"disambiguationData":[TD([[makeQuery(id+"F0.imprint","INTERSECT",VERTEX,{"derivedFrom":[subQ0,sQuery(id+"F0.wireOp",EDGE,"E7")]}),-1.0]])],"derivedFrom":subQ0})])],"isStart":true});}
            var Q40;
            Q40=makeQuery(id+"F1.opExtrude","CAP_EDGE",EDGE,{"disambiguationData":[OSD([sQuery(id+"F0.wireOp",EDGE,"E7")])],"isStart":true});
            var Q41;
            Q41=makeQuery(id+"F1.opExtrude","CAP_EDGE",EDGE,{"disambiguationData":[OSD([sQuery(id+"F0.wireOp",EDGE,"E6")])],"isStart":true});
            var Q42;
            {var subQ0=sQuery(id+"F0.wireOp",EDGE,"E21");Q42=makeQuery(id+"F1.opExtrude","CAP_EDGE",EDGE,{"disambiguationData":[OSD([subQ0]),TDD([makeQuery(id+"F0.imprint","IMPRINT",EDGE,{"disambiguationData":[TD([[makeQuery(id+"F0.imprint","INTERSECT",VERTEX,{"derivedFrom":[subQ0,sQuery(id+"F0.wireOp",EDGE,"E23")]}),1.0]])],"derivedFrom":subQ0})])],"isStart":true});}
            var Q43;
            Q43=makeQuery(id+"F1.opExtrude","CAP_EDGE",EDGE,{"disambiguationData":[OSD([sQuery(id+"F0.wireOp",EDGE,"E24")])],"isStart":true});
            fillet(context, id + "F2", {"entities" : qUnion([Q0, Q1, Q2, Q3, Q4, Q5, Q6, Q7, Q8, Q9, Q10, Q11, Q12, Q13, Q14, Q15, Q16, Q17, Q18, Q19, Q20, Q21, Q22, Q23, Q24, Q25, Q26, Q27, Q28, Q29, Q30, Q31, Q32, Q33, Q34, Q35, Q36, Q37, Q38, Q39, Q40, Q41, Q42, Q43]), "radius" : 0.64 * mm, "tangentPropagation" : true, "allowEdgeOverflow" : false});
        }
        {
            var Q0;
            Q0=sQuery(id+"F0.wireOp",VERTEX,"E3.start");
            var Q1;
            Q1=sQuery(id+"F0.wireOp",VERTEX,"E4.center");
            var Q2;
            Q2=sQuery(id+"F0.wireOp",VERTEX,"E34.center");
            var Q3;
            Q3=sQuery(id+"F0.wireOp",VERTEX,"E21.center");
            var Q4;
            Q4=makeQuery(id+"F1.opExtrude","SWEPT_BODY",BODY,{"disambiguationData":[OSD([sQuery(id+"F0.wireOp",EDGE,"E0"),sQuery(id+"F0.wireOp",EDGE,"E4"),sQuery(id+"F0.wireOp",EDGE,"E6"),sQuery(id+"F0.wireOp",EDGE,"E7"),sQuery(id+"F0.wireOp",EDGE,"E15"),sQuery(id+"F0.wireOp",EDGE,"E16"),sQuery(id+"F0.wireOp",EDGE,"E17"),sQuery(id+"F0.wireOp",EDGE,"E18"),sQuery(id+"F0.wireOp",EDGE,"E21"),sQuery(id+"F0.wireOp",EDGE,"E23"),sQuery(id+"F0.wireOp",EDGE,"E24"),sQuery(id+"F0.wireOp",EDGE,"E29"),sQuery(id+"F0.wireOp",EDGE,"E30"),sQuery(id+"F0.wireOp",EDGE,"E34"),sQuery(id+"F0.wireOp",EDGE,"E36"),sQuery(id+"F0.wireOp",EDGE,"E37"),sQuery(id+"F0.wireOp",EDGE,"E42"),sQuery(id+"F0.wireOp",EDGE,"E43"),sQuery(id+"F0.wireOp",EDGE,"E53"),sQuery(id+"F0.wireOp",EDGE,"E54"),sQuery(id+"F0.wireOp",EDGE,"E55"),sQuery(id+"F0.wireOp",EDGE,"E56")])]});
            hole(context, id + "F3", {"style" : HoleStyle.SIMPLE, "endStyle" : HoleEndStyle.THROUGH, "oppositeDirection" : true, "holeDiameter" : 22 * mm, "isTappedThrough" : true, "tappedDepth" : 12.7 * mm, "tapClearance" : 3, "locations" : qUnion([Q0, Q1, Q2, Q3]), "scope" : qUnion([Q4]), "majorDiameter" : 6.35 * mm});
        }
    });
